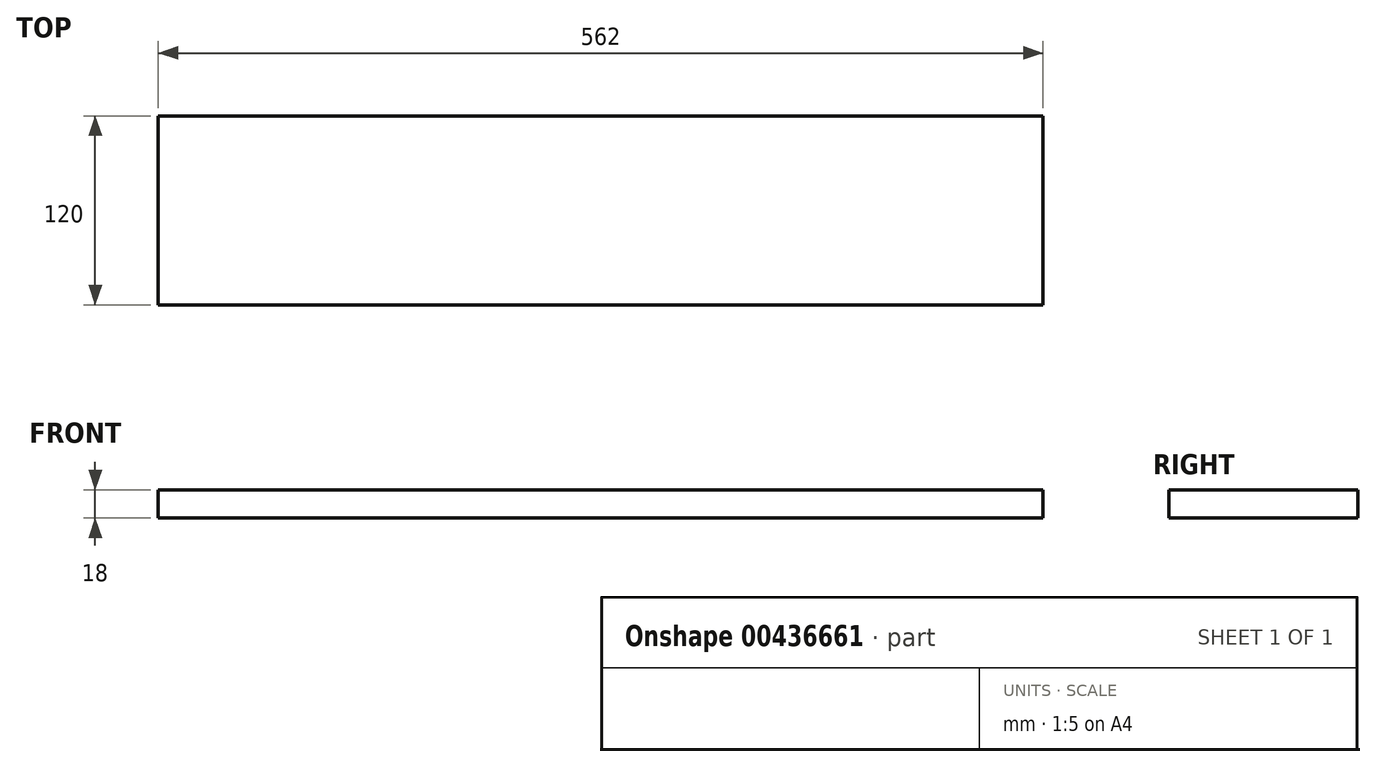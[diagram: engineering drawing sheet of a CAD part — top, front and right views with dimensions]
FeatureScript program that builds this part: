
annotation { "Feature Type Name" : "Feature", "Feature Type Description" : "" }
export const myFeature = defineFeature(function(context is Context, id is Id, definition is map)
    precondition{}
    {
        {
            var Q0;
            Q0=qCreatedBy(makeId("Right.planeOp"),FACE);
            var sketch = newSketch(context, id + "F0", { "sketchPlane" : qUnion([Q0])});
            skLineSegment(sketch, "E0.bottom", {"start": v(60, -9) * mm, "end": v(-60, -9) * mm});
            skLineSegment(sketch, "E0.top", {"start": v(60, 9) * mm, "end": v(-60, 9) * mm});
            skLineSegment(sketch, "E0.left", {"start": v(60, -9) * mm, "end": v(60, 9) * mm});
            skLineSegment(sketch, "E0.right", {"start": v(-60, -9) * mm, "end": v(-60, 9) * mm});
            skPoint(sketch, "E0.middle", {"position": v(0, 0) * mm});
            skSolve(sketch);
        }
        {
            var Q0;
            Q0=qSketchRegion(id+"F0",true);
            extrude(context, id + "F1", {"entities" : qUnion([Q0]), "depth" : 562 * mm});
        }
    });
